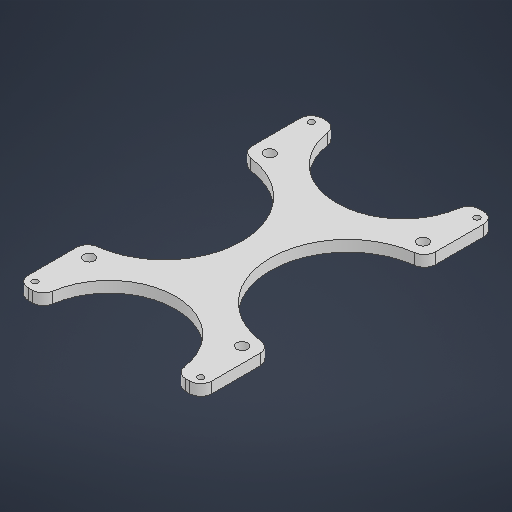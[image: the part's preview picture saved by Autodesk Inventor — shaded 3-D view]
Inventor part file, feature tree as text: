
AUTODESK INVENTOR PART (.ipt)
format: ipt  version: 2025.1 (Build 291241000, 241)  size: 556,544 bytes
history: native  units: mm
features: extrude x3, sketch x2, fillet x1, projected_geometry x1
ambient origin geometry x8: Origin, YZ Plane, XZ Plane, XY Plane, X Axis, Y Axis, Z Axis, Center Point
bodies: Solid1 (feature_tree)
feature tree (7):
  sketch  "Sketch1"  dims[d0=163.6mm d1=5.5mm d2=138.6mm d3=69.3mm]
  extrude  "Extrusion1"  Depth=69.3mm
  extrude  "Extrusion2"  Depth=10.0mm
  extrude  "Extrusion3"  Depth=10.0mm
  fillet  "Fillet1"  Radius=8.0mm
  sketch  "Sketch2"  dims[d4=5.5mm d5=10.0mm d7=250.0mm d8=8.0mm d9=8.0mm d10=8.0mm d11=8.0mm d12=8.0mm d13=150.0mm d14=10.0mm d15=0.0mm d16=3.0mm d17=0.0mm d18=70.0mm d19=60.0mm d20=10.0mm d21=0.0mm d22=10.0mm]
  projected_geometry  "Projected Loop1"
